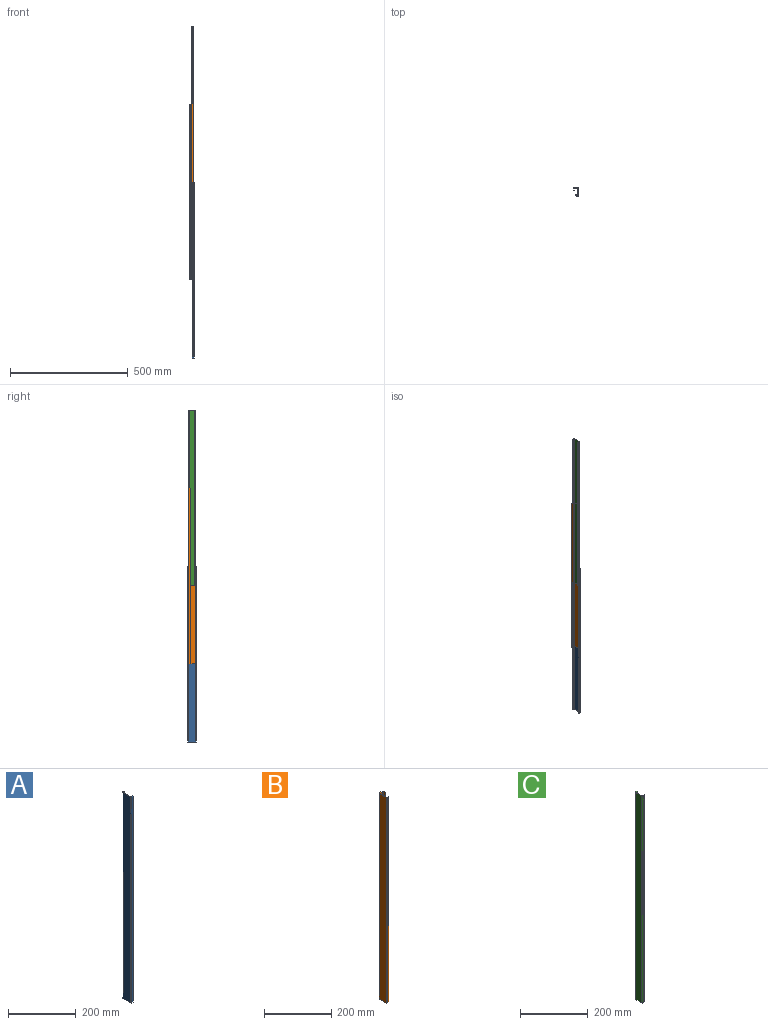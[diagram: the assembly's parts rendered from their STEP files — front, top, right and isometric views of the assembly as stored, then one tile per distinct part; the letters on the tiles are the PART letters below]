
ASSEMBLY  parts=3 mates=2
PART A: 14 faces, bbox 9x37x747 mm
  f0: plane 747x6mm, normal (0,1,0), area 4482mm2, adj f1,f11,f12,f13
  f1: cylinder r=1.5mm len=747mm, axis (0,0,-1), area 1760.1mm2, adj f0,f2,f12,f13
  f2: plane 747x31mm, normal (1,0,0), area 23157mm2, adj f1,f3,f12,f13
  f3: cylinder r=1.5mm len=747mm, axis (0,0,-1), area 1760.1mm2, adj f2,f4,f12,f13
  f4: plane 747x6mm, normal (0,-1,0), area 4482mm2, adj f3,f5,f12,f13
  f5: plane 747x1.5mm, normal (1,0,0), area 1120.5mm2, adj f4,f6,f12,f13
  f6: plane 747x6mm, normal (0,1,0), area 4482mm2, adj f5,f7,f12,f13
  f7: cylinder r=3mm len=747mm, axis (0,0,-1), area 3520.2mm2, adj f6,f8,f12,f13
  f8: plane 747x31mm, normal (-1,0,0), area 23157mm2, adj f7,f9,f12,f13
  f9: cylinder r=3mm len=747mm, axis (0,0,-1), area 3520.2mm2, adj f8,f10,f12,f13
  f10: plane 747x6mm, normal (0,-1,0), area 4482mm2, adj f9,f11,f12,f13
  f11: plane 747x1.5mm, normal (1,0,0), area 1120.5mm2, adj f0,f10,f12,f13
  f12: plane 37x9mm, normal (0,0,1), area 75.1mm2, adj f0,f1,f2,f3,f4,f5,f6,f7
  f13: plane 37x9mm, normal (0,0,-1), area 75.1mm2, adj f0,f1,f2,f3,f4,f5,f6,f7
PART B: 18 faces, bbox 17x33x747 mm
  f0: cylinder r=1mm len=747mm, axis (0,0,-1), area 1173.4mm2, adj f1,f15,f16,f17
  f1: plane 747x8.5mm, normal (-1,0,0), area 6349.5mm2, adj f0,f2,f16,f17
  f2: plane 747x1.5mm, normal (0,-1,0), area 1120.5mm2, adj f1,f3,f16,f17
  f3: plane 747x8.5mm, normal (1,0,0), area 6349.5mm2, adj f2,f4,f16,f17
  f4: cylinder r=2.5mm len=747mm, axis (0,0,-1), area 2933.5mm2, adj f3,f5,f16,f17
  f5: plane 747x12mm, normal (0,1,0), area 8964mm2, adj f4,f6,f16,f17
  f6: cylinder r=2.5mm len=747mm, axis (0,0,-1), area 2933.5mm2, adj f5,f7,f16,f17
  f7: plane 747x28mm, normal (-1,0,0), area 20916mm2, adj f6,f8,f16,f17
  f8: cylinder r=2.5mm len=747mm, axis (0,0,-1), area 2933.5mm2, adj f7,f9,f16,f17
  f9: plane 747x7mm, normal (0,-1,0), area 5229mm2, adj f8,f10,f16,f17
  f10: plane 747x1.5mm, normal (1,0,0), area 1120.5mm2, adj f9,f11,f16,f17
  f11: plane 747x7mm, normal (0,1,0), area 5229mm2, adj f10,f12,f16,f17
  f12: cylinder r=1mm len=747mm, axis (0,0,-1), area 1173.4mm2, adj f11,f13,f16,f17
  f13: plane 747x28mm, normal (1,0,0), area 20916mm2, adj f12,f14,f16,f17
  f14: cylinder r=1mm len=747mm, axis (0,0,-1), area 1173.4mm2, adj f13,f15,f16,f17
  f15: plane 747x12mm, normal (0,-1,0), area 8964mm2, adj f0,f14,f16,f17
  f16: plane 33x17mm, normal (0,0,1), area 95.6mm2, adj f0,f1,f2,f3,f4,f5,f6,f7
  f17: plane 33x17mm, normal (0,0,-1), area 95.6mm2, adj f0,f1,f2,f3,f4,f5,f6,f7
PART C: 14 faces, bbox 9x30x747 mm
  f0: cylinder r=1.5mm len=747mm, axis (0,0,-1), area 1760.1mm2, adj f1,f11,f12,f13
  f1: plane 747x6mm, normal (0,-1,0), area 4482mm2, adj f0,f2,f12,f13
  f2: plane 747x1.5mm, normal (1,0,0), area 1120.5mm2, adj f1,f3,f12,f13
  f3: plane 747x6mm, normal (0,1,0), area 4482mm2, adj f2,f4,f12,f13
  f4: cylinder r=3mm len=747mm, axis (0,0,-1), area 3520.2mm2, adj f3,f5,f12,f13
  f5: plane 747x24mm, normal (-1,0,0), area 17928mm2, adj f4,f6,f12,f13
  f6: cylinder r=3mm len=747mm, axis (0,0,-1), area 3520.2mm2, adj f5,f7,f12,f13
  f7: plane 747x6mm, normal (0,-1,0), area 4482mm2, adj f6,f8,f12,f13
  f8: plane 747x1.5mm, normal (1,0,0), area 1120.5mm2, adj f7,f9,f12,f13
  f9: plane 747x6mm, normal (0,1,0), area 4482mm2, adj f8,f10,f12,f13
  f10: cylinder r=1.5mm len=747mm, axis (0,0,-1), area 1760.1mm2, adj f9,f11,f12,f13
  f11: plane 747x24mm, normal (1,0,0), area 17928mm2, adj f0,f10,f12,f13
  f12: plane 30x9mm, normal (0,0,1), area 64.6mm2, adj f0,f1,f2,f3,f4,f5,f6,f7
  f13: plane 30x9mm, normal (0,0,-1), area 64.6mm2, adj f0,f1,f2,f3,f4,f5,f6,f7
PLACE A rot(axis=(0,0,1),180deg) t=(123.29,-18.88,-22.32)mm fixed
PLACE B rot(axis=(0,1,0),180deg) t=(121.34,-18.88,309.85)mm
PLACE C rot(axis=(0,0,1),180deg) t=(119.84,-18.88,268.52)mm
MATE slider A.f12 <-> B.f17  axis (0,0,1) through (117.29,-0.38,351.18)mm
MATE slider B.f17 <-> C.f12  axis (0,0,1) through (115.79,-15.69,683.35)mm
